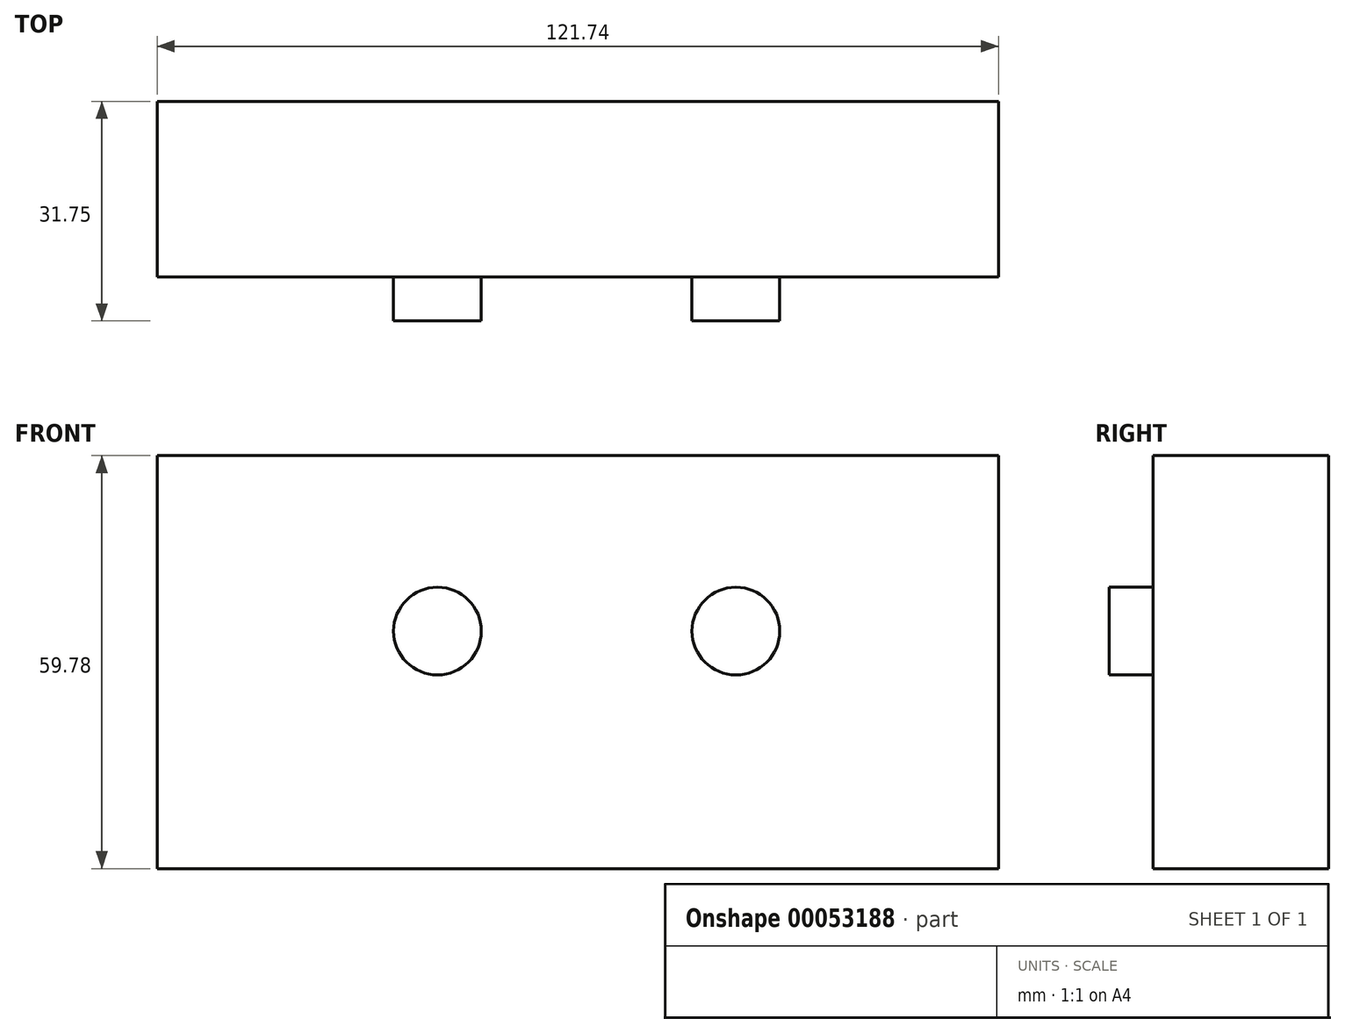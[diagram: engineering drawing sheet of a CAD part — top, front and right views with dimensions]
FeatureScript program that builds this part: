
annotation { "Feature Type Name" : "Feature", "Feature Type Description" : "" }
export const myFeature = defineFeature(function(context is Context, id is Id, definition is map)
    precondition{}
    {
        {
            var Q0;
            Q0=qCreatedBy(makeId("Front.planeOp"),FACE);
            var sketch = newSketch(context, id + "F0", { "sketchPlane" : qUnion([Q0])});
            skLineSegment(sketch, "E0.bottom", {"start": v(-33.85, 25.4) * mm, "end": v(37.09, 25.4) * mm});
            skLineSegment(sketch, "E0.top", {"start": v(-33.85, -34.37) * mm, "end": v(37.09, -34.37) * mm});
            skLineSegment(sketch, "E0.left", {"start": v(-33.85, 25.4) * mm, "end": v(-33.85, -34.37) * mm});
            skLineSegment(sketch, "E0.right", {"start": v(37.09, 25.4) * mm, "end": v(37.09, -34.37) * mm});
            skLineSegment(sketch, "E1", {"start": v(-18.69, 14.88) * mm, "end": v(-18.69, -23.47) * mm, "construction": true});
            skLineSegment(sketch, "E2", {"start": v(24.5, 15) * mm, "end": v(24.5, -22.84) * mm, "construction": true});
            skCircle(sketch, "E3", {"center": v(-18.69, 0) * mm, "radius": 6.35 * mm});
            skCircle(sketch, "E4", {"center": v(24.5, 0) * mm, "radius": 6.35 * mm});
            skSolve(sketch);
        }
        {
            var Q0;
            Q0=makeQuery(id+"F0.imprint","IMPRINT",FACE,{"disambiguationData":[TD([[makeQuery(id+"F0.imprint","IMPRINT",EDGE,{"derivedFrom":sQuery(id+"F0.wireOp",EDGE,"E0.bottom")}),-1.0]])]});
            var Q1;
            Q1=makeQuery(id+"F0.imprint","IMPRINT",FACE,{"disambiguationData":[TD([[makeQuery(id+"F0.imprint","IMPRINT",EDGE,{"derivedFrom":sQuery(id+"F0.wireOp",EDGE,"E3")}),1.0]])]});
            var Q2;
            Q2=makeQuery(id+"F0.imprint","IMPRINT",FACE,{"disambiguationData":[TD([[makeQuery(id+"F0.imprint","IMPRINT",EDGE,{"derivedFrom":sQuery(id+"F0.wireOp",EDGE,"E4")}),1.0]])]});
            extrude(context, id + "F1", {"entities" : qUnion([Q0, Q1, Q2]), "oppositeDirection" : true, "depth" : 25.4 * mm});
        }
        {
            var Q0;
            Q0=makeQuery(id+"F0.imprint","IMPRINT",FACE,{"disambiguationData":[TD([[makeQuery(id+"F0.imprint","IMPRINT",EDGE,{"derivedFrom":sQuery(id+"F0.wireOp",EDGE,"E3")}),1.0]])]});
            var Q1;
            Q1=makeQuery(id+"F0.imprint","IMPRINT",FACE,{"disambiguationData":[TD([[makeQuery(id+"F0.imprint","IMPRINT",EDGE,{"derivedFrom":sQuery(id+"F0.wireOp",EDGE,"E4")}),1.0]])]});
            extrude(context, id + "F2", {"entities" : qUnion([Q0, Q1]), "operationType" : NewBodyOperationType.ADD, "depth" : 6.35 * mm});
        }
        {
            var Q0;
            Q0=makeQuery(id+"F1.opExtrude","SWEPT_FACE",FACE,{"disambiguationData":[OSD([sQuery(id+"F0.wireOp",EDGE,"E0.right")])]});
            extrude(context, id + "F3", {"entities" : qUnion([Q0]), "operationType" : NewBodyOperationType.ADD, "depth" : 25.4 * mm});
        }
        {
            var Q0;
            Q0=makeQuery(id+"F1.opExtrude","SWEPT_FACE",FACE,{"disambiguationData":[OSD([sQuery(id+"F0.wireOp",EDGE,"E0.left")])]});
            extrude(context, id + "F4", {"entities" : qUnion([Q0]), "operationType" : NewBodyOperationType.ADD, "depth" : 25.4 * mm});
        }
    });
